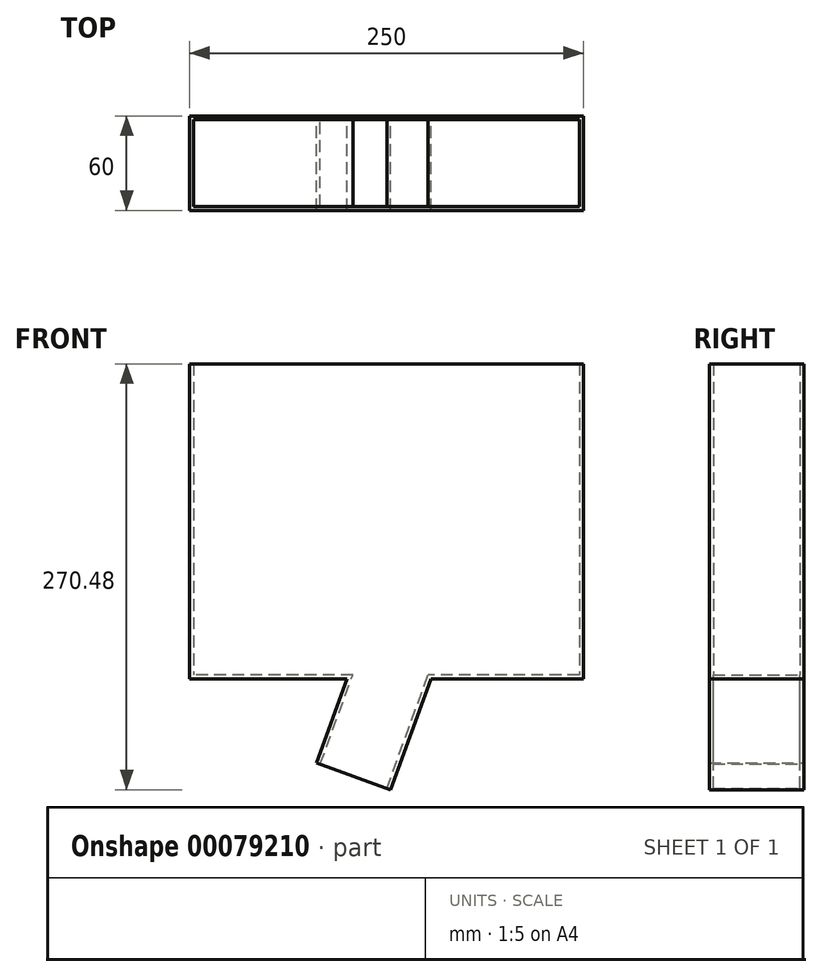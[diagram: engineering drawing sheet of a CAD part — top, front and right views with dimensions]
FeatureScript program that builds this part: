
annotation { "Feature Type Name" : "Feature", "Feature Type Description" : "" }
export const myFeature = defineFeature(function(context is Context, id is Id, definition is map)
    precondition{}
    {
        {
            var Q0;
            Q0=qCreatedBy(makeId("Front.planeOp"),FACE);
            var sketch = newSketch(context, id + "F0", { "sketchPlane" : qUnion([Q0])});
            skLineSegment(sketch, "E0.bottom", {"start": v(125, 100) * mm, "end": v(-125, 100) * mm});
            skLineSegment(sketch, "E0.top", {"start": v(125, -100) * mm, "end": v(28.2, -100) * mm});
            skLineSegment(sketch, "E0.left", {"start": v(125, 100) * mm, "end": v(125, -100) * mm});
            skLineSegment(sketch, "E0.right", {"start": v(-125, 100) * mm, "end": v(-125, -100) * mm});
            skPoint(sketch, "E0.middle", {"position": v(0, 0) * mm});
            skLineSegment(sketch, "E1", {"start": v(2.56, 0) * mm, "end": v(0, 0) * mm, "construction": true});
            skLineSegment(sketch, "E2", {"start": v(2.56, 0) * mm, "end": v(2.56, -170.48) * mm, "construction": true});
            skLineSegment(sketch, "E3", {"start": v(2.56, -170.48) * mm, "end": v(28.2, -100) * mm});
            skLineSegment(sketch, "E4", {"start": v(2.56, -170.48) * mm, "end": v(-44.43, -153.38) * mm});
            skLineSegment(sketch, "E5", {"start": v(-44.43, -153.38) * mm, "end": v(-25, -100) * mm});
            skLineSegment(sketch, "E6.trimOffspring", {"start": v(-25, -100) * mm, "end": v(-125, -100) * mm});
            skSolve(sketch);
        }
        {
            var Q0;
            Q0=makeQuery(id+"F0.imprint","IMPRINT",FACE,{"disambiguationData":[TD([[makeQuery(id+"F0.imprint","IMPRINT",EDGE,{"derivedFrom":sQuery(id+"F0.wireOp",EDGE,"E0.bottom")}),1.0]])]});
            extrude(context, id + "F1", {"entities" : qUnion([Q0]), "depth" : 60 * mm});
        }
        {
            var Q0;
            Q0=makeQuery(id+"F1.opExtrude","SWEPT_FACE",FACE,{"disambiguationData":[OSD([sQuery(id+"F0.wireOp",EDGE,"E0.bottom")])]});
            var Q1;
            Q1=makeQuery(id+"F1.opExtrude","SWEPT_FACE",FACE,{"disambiguationData":[OSD([sQuery(id+"F0.wireOp",EDGE,"E4")])]});
            shell(context, id + "F2", {"entities" : qUnion([Q0, Q1]), "thickness" : 2.5 * mm});
        }
    });
